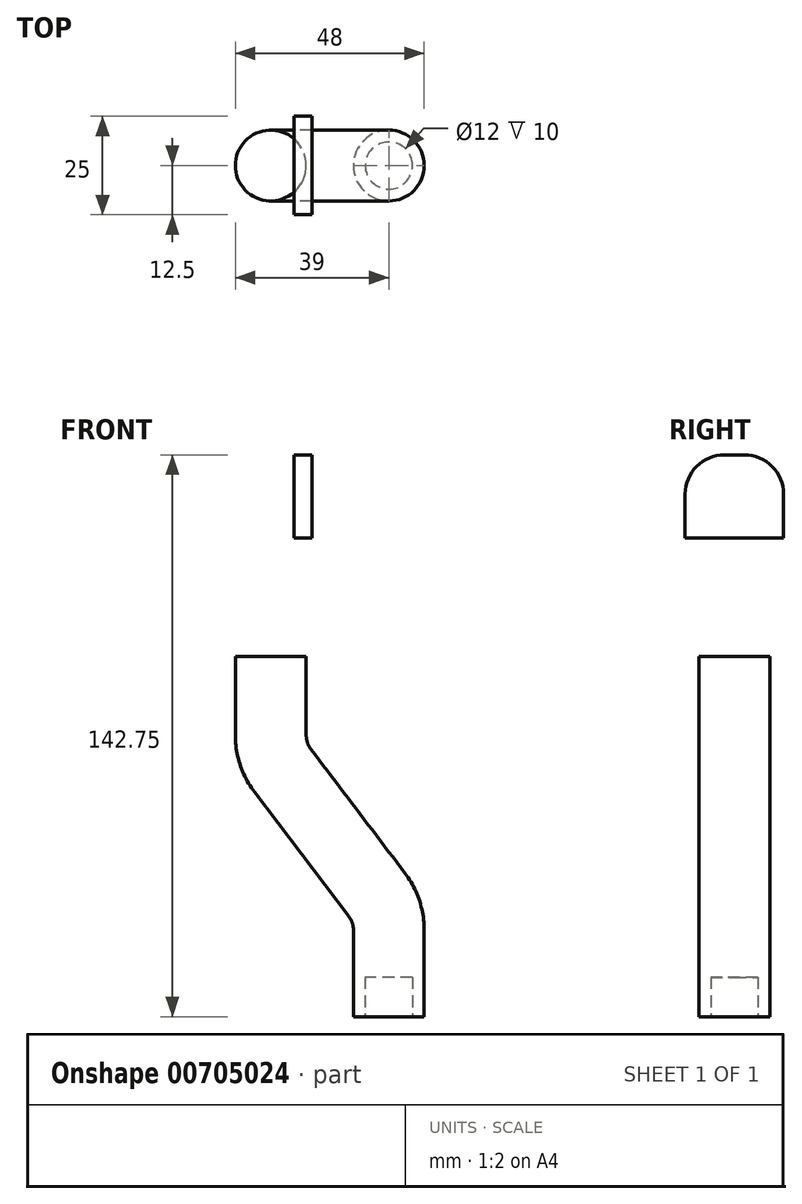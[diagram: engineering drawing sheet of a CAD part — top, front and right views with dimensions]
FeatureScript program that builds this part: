
annotation { "Feature Type Name" : "Feature", "Feature Type Description" : "" }
export const myFeature = defineFeature(function(context is Context, id is Id, definition is map)
    precondition{}
    {
        {
            var Q0;
            Q0=qCreatedBy(makeId("Top.planeOp"),FACE);
            var sketch = newSketch(context, id + "F0", { "sketchPlane" : qUnion([Q0])});
            skCircle(sketch, "E0", {"center": v(0, 0) * mm, "radius": 9 * mm});
            skSolve(sketch);
        }
        {
            var Q0;
            Q0=qCreatedBy(makeId("Front.planeOp"),FACE);
            var sketch = newSketch(context, id + "F1", { "sketchPlane" : qUnion([Q0])});
            skLineSegment(sketch, "E1", {"start": v(0, 0) * mm, "end": v(0, 21.92) * mm});
            skLineSegment(sketch, "E2", {"start": v(-3.05, 30.99) * mm, "end": v(-26.95, 62.5) * mm});
            skLineSegment(sketch, "E3", {"start": v(-30, 71.57) * mm, "end": v(-30, 91.57) * mm});
            skPoint(sketch, "E4.visualSharp", {"position": v(0, 26.97) * mm});
            skArc(sketch, "E4.filletArc", {"start": v(0, 21.92) * mm, "mid": v(-0.78, 26.7) * mm, "end": v(-3.05, 30.99) * mm});
            skPoint(sketch, "E5.visualSharp", {"position": v(-30, 66.52) * mm});
            skArc(sketch, "E5.filletArc", {"start": v(-30, 71.57) * mm, "mid": v(-29.22, 66.79) * mm, "end": v(-26.95, 62.5) * mm});
            skLineSegment(sketch, "E6", {"start": v(0, -31.7) * mm, "end": v(0, 114) * mm, "construction": true});
            skSolve(sketch);
        }
        {
            var Q0;
            Q0=makeQuery(id+"F0.imprint","IMPRINT",FACE,{"disambiguationData":[TD([[makeQuery(id+"F0.imprint","IMPRINT",EDGE,{"derivedFrom":sQuery(id+"F0.wireOp",EDGE,"E0")}),1.0]])]});
            var Q1;
            Q1=sQuery(id+"F1.wireOp",EDGE,"E2");
            var Q2;
            Q2=sQuery(id+"F1.wireOp",EDGE,"E5.filletArc");
            var Q3;
            Q3=sQuery(id+"F1.wireOp",EDGE,"E3");
            var Q4;
            Q4=sQuery(id+"F1.wireOp",EDGE,"E4.filletArc");
            var Q5;
            Q5=sQuery(id+"F1.wireOp",EDGE,"E1");
            sweep(context, id + "F2", {"profiles" : qUnion([Q0]), "path" : qUnion([Q1, Q2, Q3, Q4, Q5])});
        }
        {
            var Q0;
            Q0=qCreatedBy(makeId("Front.planeOp"),FACE);
            var sketch = newSketch(context, id + "F3", { "sketchPlane" : qUnion([Q0])});
            skLineSegment(sketch, "E7", {"start": v(-24.1, 77.47) * mm, "end": v(-24.1, 142.6) * mm, "construction": true});
            skLineSegment(sketch, "E8.bottom", {"start": v(-24.1, 121.57) * mm, "end": v(-19.52, 121.57) * mm});
            skLineSegment(sketch, "E8.top", {"start": v(-24.1, 142.75) * mm, "end": v(-19.52, 142.75) * mm});
            skLineSegment(sketch, "E8.left", {"start": v(-24.1, 121.57) * mm, "end": v(-24.1, 142.75) * mm});
            skLineSegment(sketch, "E8.right", {"start": v(-19.52, 121.57) * mm, "end": v(-19.52, 142.75) * mm});
            skPoint(sketch, "E9.start.orphan", {"position": v(-19.52, 132.16) * mm});
            skLineSegment(sketch, "E10", {"start": v(-2.3, 132.16) * mm, "end": v(-19.52, 132.16) * mm, "construction": true});
            skSolve(sketch);
        }
        {
            var Q0;
            Q0 = qSketchRegion(id + "F3", true);
            extrude(context, id + "F4", {"entities" : qUnion([Q0]), "endBound" : BoundingType.SYMMETRIC, "depth" : 25 * mm, "offsetDistance" : 25 * mm});
        }
        {
            var Q0;
            Q0=makeQuery(id+"F2.opSweep","CAP_FACE",FACE,{"disambiguationData":[OSD([sQuery(id+"F0.wireOp",EDGE,"E0"),sQuery(id+"F1.wireOp",VERTEX,"E3.end")])],"isStart":false});
            cPlane(context, id + "F5", {"entities" : qUnion([Q0]), "cplaneType" : CPlaneType.OFFSET, "offset" : 0 * mm, "width" : 150 * mm, "height" : 150 * mm});
        }
        {
            var Q0;
            Q0=qCreatedBy(id+"F5.planeOp",FACE);
            var sketch = newSketch(context, id + "F6", { "sketchPlane" : qUnion([Q0])});
            skPoint(sketch, "E11.orphan", {"position": v(-29.8, 0) * mm});
            skArc(sketch, "E12", {"start": v(-38.15, -3.83) * mm, "mid": v(-32.3, -8.7) * mm, "end": v(-24.8, -7.34) * mm});
            skArc(sketch, "E13", {"start": v(-38.35, 3.35) * mm, "mid": v(-39, -0.26) * mm, "end": v(-38.15, -3.83) * mm});
            skArc(sketch, "E14", {"start": v(-25.97, 8.05) * mm, "mid": v(-33.2, 8.42) * mm, "end": v(-38.35, 3.35) * mm});
            skArc(sketch, "E15", {"start": v(-24.8, -7.34) * mm, "mid": v(-21.03, 0.68) * mm, "end": v(-25.97, 8.05) * mm});
            skSolve(sketch);
        }
        {
            var Q0;
            Q0=makeQuery(id+"F4.opExtrude","SWEPT_FACE",FACE,{"disambiguationData":[OSD([sQuery(id+"F3.wireOp",EDGE,"E8.bottom")])]});
            var Q1;
            Q1=makeQuery(id+"F6.imprint","IMPRINT",FACE,{"disambiguationData":[TD([[makeQuery(id+"F6.imprint","IMPRINT",EDGE,{"derivedFrom":sQuery(id+"F6.wireOp",EDGE,"E12")}),1.0]])]});
            loft(context, id + "F7", {"bodyType" : ToolBodyType.SURFACE, "wireProfilesArray" : [{ "wireProfileEntities" : qUnion([Q0]) }, { "wireProfileEntities" : qUnion([Q1]) }]});
        }
        {
            var Q0;
            Q0=qCreatedBy(makeId("Top.planeOp"),FACE);
            var sketch = newSketch(context, id + "F8", { "sketchPlane" : qUnion([Q0])});
            skCircle(sketch, "E16", {"center": v(0, 0) * mm, "radius": 6 * mm});
            skSolve(sketch);
        }
        {
            var Q0;
            Q0 = qSketchRegion(id + "F8", true);
            extrude(context, id + "F9", {"entities" : qUnion([Q0]), "operationType" : NewBodyOperationType.REMOVE, "depth" : 10 * mm, "offsetDistance" : 25 * mm});
        }
        {
            var Q0;
            Q0=makeQuery(id+"F4.opExtrude","SWEPT_FACE",FACE,{"disambiguationData":[OSD([sQuery(id+"F3.wireOp",EDGE,"E8.right")])]});
            var sketch = newSketch(context, id + "F10", { "sketchPlane" : qUnion([Q0])});
            skCircle(sketch, "E17", {"center": v(0, 164.43) * mm, "radius": 5.89 * mm});
            skSolve(sketch);
        }
        {
            var Q0;
            Q0 = qSketchRegion(id + "F10", true);
            extrude(context, id + "F11", {"entities" : qUnion([Q0]), "operationType" : NewBodyOperationType.REMOVE, "oppositeDirection" : true, "depth" : 25 * mm, "offsetDistance" : 25 * mm});
        }
        {
            var Q0;
            Q0=makeQuery(id+"F4.opExtrude","CAP_EDGE",EDGE,{"disambiguationData":[OSD([sQuery(id+"F3.wireOp",EDGE,"E8.top")])],"isStart":false});
            var Q1;
            Q1=makeQuery(id+"F4.opExtrude","CAP_EDGE",EDGE,{"disambiguationData":[OSD([sQuery(id+"F3.wireOp",EDGE,"E8.top")])],"isStart":true});
            fillet(context, id + "F12", {"entities" : qUnion([Q0, Q1]), "radius" : 10 * mm, "tangentPropagation" : true, "allowEdgeOverflow" : false});
        }
    });
